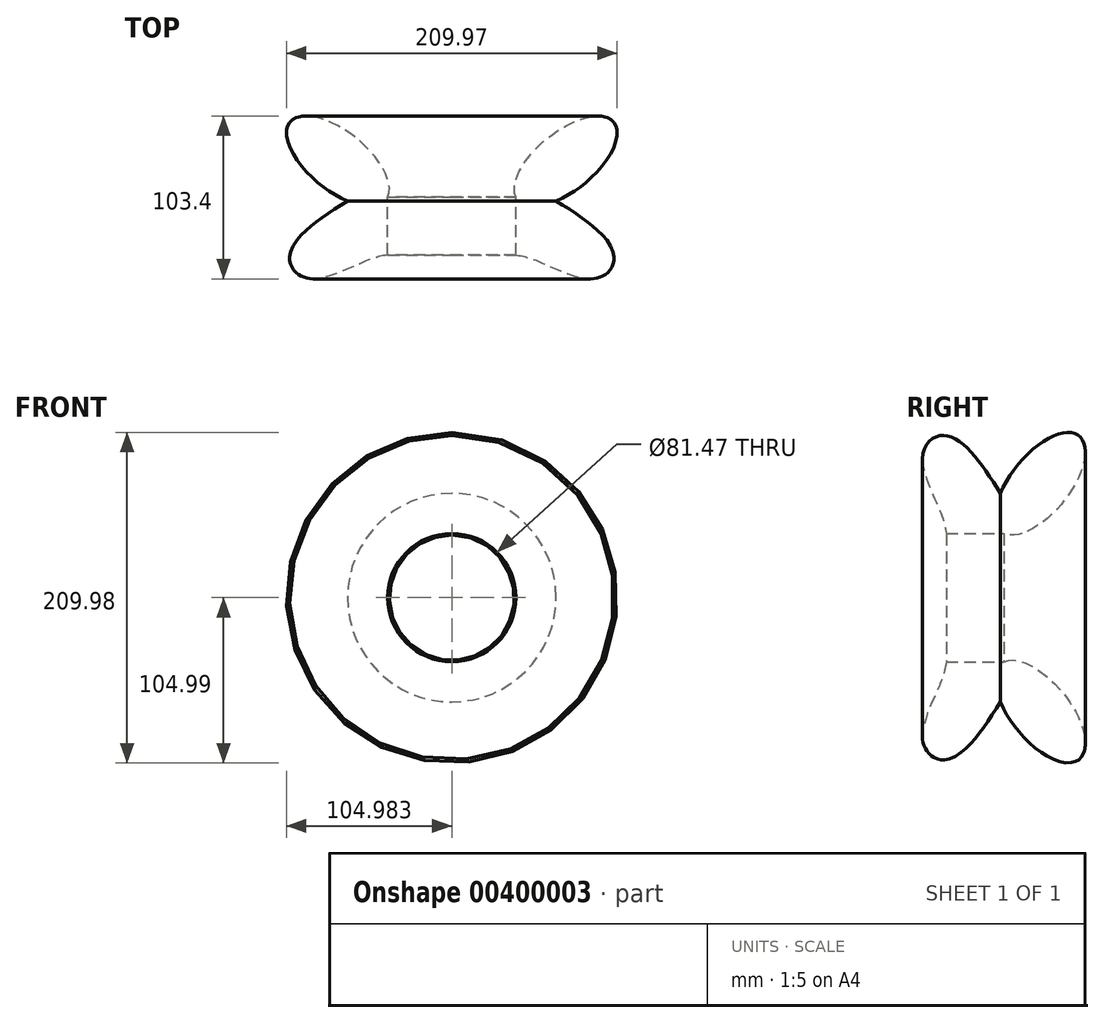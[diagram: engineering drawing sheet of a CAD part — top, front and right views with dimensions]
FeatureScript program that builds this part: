
annotation { "Feature Type Name" : "Feature", "Feature Type Description" : "" }
export const myFeature = defineFeature(function(context is Context, id is Id, definition is map)
    precondition{}
    {
        {
            var Q0;
            Q0=qCreatedBy(makeId("Top.planeOp"),FACE);
            var sketch = newSketch(context, id + "F0", { "sketchPlane" : qUnion([Q0])});
            skLineSegment(sketch, "E0", {"start": v(7.62, -22.38) * mm, "end": v(7.62, -22.4) * mm});
            skEllipticalArc(sketch, "E1", {});
            skLineSegment(sketch, "E2", {"start": v(-37.59, 51.2) * mm, "end": v(-37.59, -40.52) * mm});
            skLineSegment(sketch, "E3", {"start": v(3.15, 14.42) * mm, "end": v(3.15, -22.38) * mm});
            skFitSpline(sketch, "E4", {"points": [v(28.67, 12.06) * mm, v(58.62, -10.35) * mm, v(65.2, -26.9) * mm, v(52.06, -37.4) * mm, v(15.56, -25.58) * mm, v(3.15, -22.38) * mm], "startDerivative": vector(135.77, -86.13) * mm, "endDerivative": vector(-69.4, 10.26) * mm});
            const initialGuessF0  = {"E1": [0.034747201949357986, 0.037337999790906906, 0.777063856648589, 0.6294217685228413, 0.039224577054988885, 0.018602634742264663, 4.1584342825886775, 3.029566952323356]};
            skSetInitialGuess(sketch, initialGuessF0);
            skSolve(sketch);
        }
        {
            var Q0;
            Q0=makeQuery(id+"F0.imprint","IMPRINT",FACE,{"disambiguationData":[TD([[makeQuery(id+"F0.imprint","IMPRINT",EDGE,{"derivedFrom":sQuery(id+"F0.wireOp",EDGE,"E1")}),1.0]])]});
            var Q1;
            Q1=sQuery(id+"F0.wireOp",EDGE,"E2");
            revolve(context, id + "F1", {"entities" : qUnion([Q0]), "axis" : qUnion([Q1]), "revolveType" : RevolveType.FULL});
        }
    });
